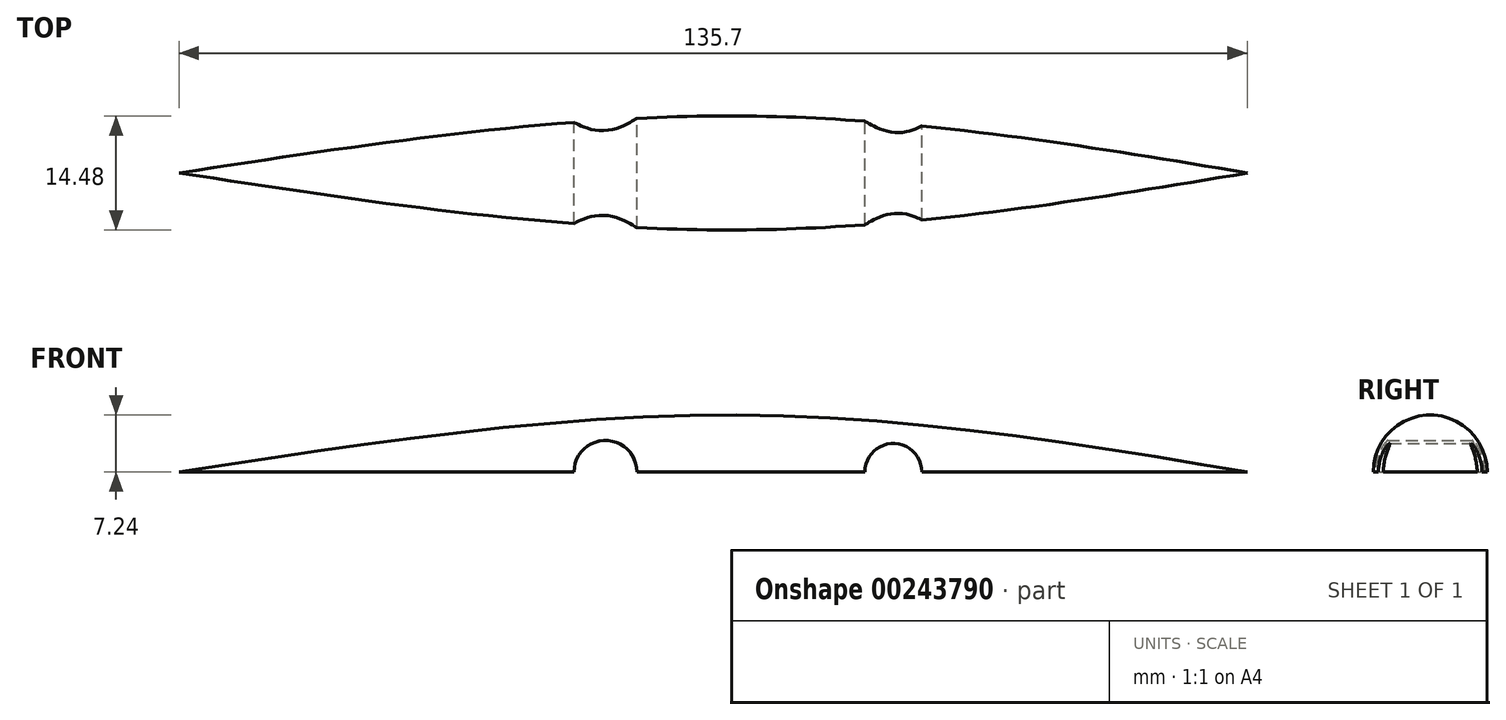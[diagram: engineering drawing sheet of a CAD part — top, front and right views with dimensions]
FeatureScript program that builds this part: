
annotation { "Feature Type Name" : "Feature", "Feature Type Description" : "" }
export const myFeature = defineFeature(function(context is Context, id is Id, definition is map)
    precondition{}
    {
        {
            var Q0;
            Q0=qCreatedBy(makeId("Top.planeOp"),FACE);
            var sketch = newSketch(context, id + "F0", { "sketchPlane" : qUnion([Q0])});
            skFitSpline(sketch, "E0", {"points": [v(0, 0) * mm, v(71, 7.24) * mm, v(135.7, 0) * mm], "startDerivative": vector(140.44, 21.55) * mm, "endDerivative": vector(130.9, -21.88) * mm});
            skLineSegment(sketch, "E1", {"start": v(0, 0) * mm, "end": v(135.7, 0) * mm});
            skSolve(sketch);
        }
        {
            var Q0;
            Q0 = qSketchRegion(id + "F0", true);
            var Q1;
            Q1=sQuery(id+"F0.wireOp",EDGE,"E1");
            var Q2;
            Q2=sQuery(id+"F0.wireOp",EDGE,"E1");
            revolve(context, id + "F1", {"entities" : qUnion([Q0]), "surfaceEntities" : qUnion([Q1]), "axis" : qUnion([Q2]), "revolveType" : RevolveType.ONE_DIRECTION, "angle" : 180 * degree});
        }
        {
            var Q0;
            Q0=qCreatedBy(makeId("Front.planeOp"),FACE);
            var sketch = newSketch(context, id + "F2", { "sketchPlane" : qUnion([Q0])});
            skCircle(sketch, "E2", {"center": v(54.18, 0) * mm, "radius": 4 * mm});
            skCircle(sketch, "E3", {"center": v(90.74, 0) * mm, "radius": 3.61 * mm});
            skSolve(sketch);
        }
        {
            var Q0;
            Q0 = qSketchRegion(id + "F2", true);
            extrude(context, id + "F3", {"entities" : qUnion([Q0]), "operationType" : NewBodyOperationType.REMOVE, "endBound" : BoundingType.THROUGH_ALL, "depth" : 152.4 * mm, "hasSecondDirection" : true, "secondDirectionOppositeDirection" : true, "secondDirectionDepth" : 25.4 * mm});
        }
    });
